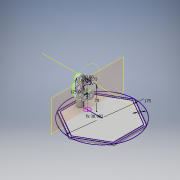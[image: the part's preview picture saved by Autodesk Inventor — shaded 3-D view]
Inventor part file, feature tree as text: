
AUTODESK INVENTOR PART (.ipt)
format: ipt  version: 2019 (Build 230136000, 136)  size: 250,880 bytes
history: native  units: mm
features: sketch x6, extrude x5, revolve x1, mirror x1, other x1, sweep x1, fillet x1, plane x1, projected_geometry x1
ambient origin geometry x8: Origin, YZ Plane, XZ Plane, XY Plane, X Axis, Y Axis, Z Axis, Center Point
bodies: Solid1 (feature_tree)
feature tree (18):
  sketch  "Sketch2"  dims[d1=38.9815mm d2=180.0deg]
  revolve  "Revolution1"  Angle=180.0deg
  sketch  "Sketch3"  dims[d3=6.75mm d4=4.0mm]
  extrude  "Extrusion3"  Depth=4.0mm
  extrude  "Extrusion4"  Depth=9.599311mm
  extrude  "Extrusion6"  Depth=5.0mm
  mirror  "Mirror2"
  other  "Work Axis3"
  sweep  "Sweep1"
  fillet  "Fillet4"  Radius=0.4mm
  plane  "Work Plane1"
  sketch  "Sketch8"  dims[d16=5.0mm d17=0.0mm d18=2.0mm d19=0.0mm d27=0.4mm d28=0.0mm]
  sketch  "Sketch10"  dims[d32=90.0deg d33=0.0mm d34=0.0mm d36=4.0mm d38=11.0mm d39=4.0mm d40=50.0mm d42=21.816616mm d44=10.0mm d45=0.0mm d47=10.0mm d48=0.0mm]
  extrude  "Extrusion7"  TaperAngle=0.0deg  [1 undecoded]
  extrude  "Extrusion8"  Depth=4.0mm
  sketch  "Sketch5"  dims[d5=70.0mm d11=9.599311mm]
  projected_geometry  "Projected Loop2"
  sketch  "Sketch7"  dims[d14=175.0mm d15=5.0mm]
note: 1 required parameter value undecoded (feature->parameter linkage not recoverable at this tier; creation-order binding heuristic only, values carry confidence <= 0.55)
